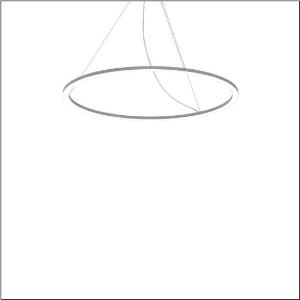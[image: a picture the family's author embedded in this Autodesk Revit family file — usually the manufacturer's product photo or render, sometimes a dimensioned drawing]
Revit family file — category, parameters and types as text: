
# Revit family: silica_r__21_ring-d_5pjbd3d1204a_4b66
name_source: partatom
category: Lighting Fixtures
units: mm (PartAtom-declared; Revit-internal decimal feet)

## family parameters
Cut with Voids When Loaded = No
Host = Face
Light Source = No
Part Type = Normal
Room Calculation Point = No
Round Connector Dimension = Use Diameter
Shared = No

## types (1)
- Silica® 21 Ring-D (1 x LED, 8050 lm, 94 W, 3000K)
    Apparent Load = 94 VA
    CIE Flux Codes = 37 69 92 100 100
    Color Rendering = 80
    Color Temperature = 3000K
    Default Elevation = 1800 mm
    Description = Silica® 21 Ring-D, suspended luminaire, of PMMA, frosted, light emission: ring underside luminous distribution, primary light characteristic: symmetric, installation type: suspended mounting, LED, rated luminous flux: 8.050lm, luminous efficacy: 86lm/W, light colour: 830, colour temperature: 3000K, with terminal, 5-pole, mains connection: 230V, AC/DC, 0/50..60Hz, rated input power: 94W, housing, of extruded aluminium section, metallic grey (RAL 9006), diameter: 1.100mm, ceiling canopy, metallic grey (RAL 9006), protection rating (lamp compartment): IP40, insulation class (complete): insulation class I (protective earthing), certification: CE, impact resistance: IK02, permissible operating ambient temperature: 0..+35°C, packaging unit: 1 piece
    Height = 25 mm  [stored 0.082021 ft]
    Lamp = 1 x LED
    Lamp Light Flux = 8050 lm
    Lamp Power = 94 W
    Lamp count = 1
    Length = 1100 mm
    Luminous efficacy = 86 lm/W
    Manufacturer = Siteco
    ModVariant = No
    Model = 5PJBD3D1204A
    Mounting Place = Ceiling
    Mounting Type = Pendant
    Number of Poles = 1
    OnlyDefault = Yes
    Power Factor = 1
    Product Name = Silica® 21 Ring-D
    Product group = suspended luminaire
    ProductGroupID = 904
    Protection Class = Protection class I
    Protection Degree = Degree of protection
    RLX_Detail_Level = 1
    RLX_Emergency_Light_Flux = 0 lm
    RLX_Emergency_Type = 0
    RLX_Emergency_Type_DB = No
    RlxData = <blob elided: 14557 chars, md5=6c9844d7>
    Socket = socket
    Standby Power = 0 W
    System Light Flux = 8050 lm
    System Power = 94 W
    Type Comments = Product without accessories
    Type Image = l_1251746.jpg
    URL = http://relux.com
    VarID = ---
    Voltage = 0 V
    Weight = 0.00 kg
    Width = 0 mm  [stored 0 ft]

note: [stored X ft] marks values corroborated as IEEE doubles in the binary element streams (Revit-internal decimal feet)

## geometry (parser evidence)
native form markers: Sweep x12
no freeform markers — native parametric forms only
